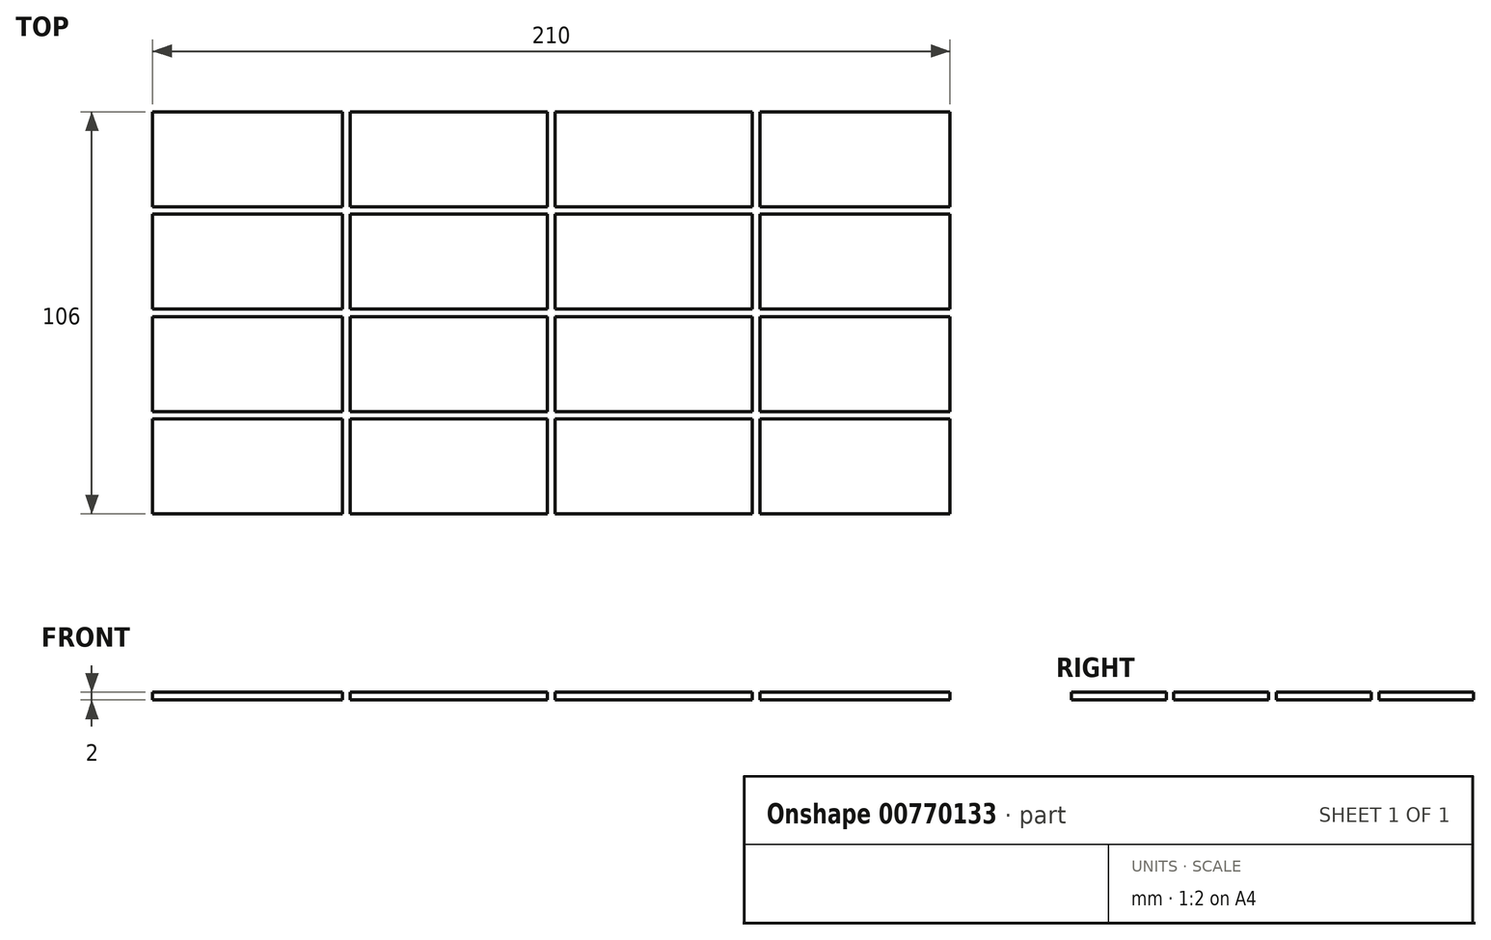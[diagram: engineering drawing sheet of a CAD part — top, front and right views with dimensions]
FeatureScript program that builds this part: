
annotation { "Feature Type Name" : "Feature", "Feature Type Description" : "" }
export const myFeature = defineFeature(function(context is Context, id is Id, definition is map)
    precondition{}
    {
        {
            var Q0;
            Q0=qCreatedBy(makeId("Top.planeOp"),FACE);
            var sketch = newSketch(context, id + "F0", { "sketchPlane" : qUnion([Q0])});
            skLineSegment(sketch, "E0.bottom", {"start": v(-107, 55) * mm, "end": v(-57, 55) * mm});
            skLineSegment(sketch, "E0.left", {"start": v(-107, 55) * mm, "end": v(-107, 30) * mm});
            skLineSegment(sketch, "E1.bottom", {"start": v(-105, 53) * mm, "end": v(-55, 53) * mm});
            skLineSegment(sketch, "E1.top", {"start": v(-105, 1) * mm, "end": v(-55, 1) * mm});
            skLineSegment(sketch, "E1.left", {"start": v(-105, 53) * mm, "end": v(-105, 28) * mm});
            skLineSegment(sketch, "E1.right", {"start": v(-1, 53) * mm, "end": v(-1, 28) * mm});
            skLineSegment(sketch, "E2", {"start": v(0, 75.4) * mm, "end": v(0, 57) * mm, "construction": true});
            skLineSegment(sketch, "E3.top", {"start": v(-57, 57) * mm, "end": v(-51, 57) * mm});
            skLineSegment(sketch, "E3.left", {"start": v(-57, 55) * mm, "end": v(-57, 57) * mm});
            skLineSegment(sketch, "E3.right", {"start": v(-51, 55) * mm, "end": v(-51, 57) * mm});
            skLineSegment(sketch, "E4.bottom", {"start": v(-42.1, 55) * mm, "end": v(-30.4, 55) * mm});
            skLineSegment(sketch, "E5.top", {"start": v(-3, 57) * mm, "end": v(0, 57) * mm});
            skLineSegment(sketch, "E5.left", {"start": v(-3, 55) * mm, "end": v(-3, 57) * mm});
            skPoint(sketch, "E4.right.end.orphan", {"position": v(-30.4, 57) * mm});
            skLineSegment(sketch, "E6.trimOffspring", {"start": v(-51, 55) * mm, "end": v(-3, 55) * mm});
            skPoint(sketch, "E7", {"position": v(-55, 53) * mm});
            skPoint(sketch, "E8", {"position": v(-53, 53) * mm});
            skLineSegment(sketch, "E9", {"start": v(-55, 53) * mm, "end": v(-55, 28) * mm});
            skLineSegment(sketch, "E10", {"start": v(-53, 53) * mm, "end": v(-53, 28) * mm});
            skPoint(sketch, "E10.endSnap0", {"position": v(-53, 1) * mm});
            skLineSegment(sketch, "E11.trimOffspring", {"start": v(-53, 1) * mm, "end": v(-1, 1) * mm});
            skLineSegment(sketch, "E12", {"start": v(-55, 53) * mm, "end": v(-55, 55) * mm});
            skLineSegment(sketch, "E13", {"start": v(-55, 55) * mm, "end": v(-53, 55) * mm});
            skLineSegment(sketch, "E14", {"start": v(-53, 55) * mm, "end": v(-53, 53) * mm});
            skLineSegment(sketch, "E15.trimOffspring", {"start": v(-53, 53) * mm, "end": v(-1, 53) * mm});
            skLineSegment(sketch, "E16", {"start": v(-1, 53) * mm, "end": v(-1, 55) * mm});
            skPoint(sketch, "E16.endSnap0", {"position": v(-27, 55) * mm});
            skLineSegment(sketch, "E17", {"start": v(-1, 55) * mm, "end": v(0, 55) * mm});
            skPoint(sketch, "E18", {"position": v(-105, 28) * mm});
            skLineSegment(sketch, "E19.bottom", {"start": v(-107, 30) * mm, "end": v(-109, 30) * mm});
            skLineSegment(sketch, "E19.top", {"start": v(-107, 24) * mm, "end": v(-109, 24) * mm});
            skLineSegment(sketch, "E19.left", {"start": v(-107, 28) * mm, "end": v(-107, 26) * mm});
            skLineSegment(sketch, "E19.right", {"start": v(-109, 30) * mm, "end": v(-109, 24) * mm});
            skLineSegment(sketch, "E20.left", {"start": v(-105, 53) * mm, "end": v(-105, 30) * mm});
            skLineSegment(sketch, "E20.right", {"start": v(-107, 53) * mm, "end": v(-107, 30) * mm});
            skLineSegment(sketch, "E21", {"start": v(-107, 28) * mm, "end": v(-55, 28) * mm});
            skLineSegment(sketch, "E22", {"start": v(-107, 26) * mm, "end": v(-55, 26) * mm});
            skLineSegment(sketch, "E23.trimOffspring", {"start": v(-105, 26) * mm, "end": v(-105, 1) * mm});
            skLineSegment(sketch, "E24.trimOffspring", {"start": v(-107, 24) * mm, "end": v(-107, 3) * mm});
            skLineSegment(sketch, "E25.trimOffspring", {"start": v(-107, 0) * mm, "end": v(-145.29, 0) * mm, "construction": true});
            skLineSegment(sketch, "E26.trimOffspring", {"start": v(-53, 26) * mm, "end": v(-1, 26) * mm});
            skLineSegment(sketch, "E27.trimOffspring", {"start": v(-53, 28) * mm, "end": v(-1, 28) * mm});
            skLineSegment(sketch, "E28.trimOffspring", {"start": v(-55, 26) * mm, "end": v(-55, 1) * mm});
            skLineSegment(sketch, "E29.trimOffspring", {"start": v(-53, 26) * mm, "end": v(-53, 1) * mm});
            skLineSegment(sketch, "E30.trimOffspring", {"start": v(-1, 26) * mm, "end": v(-1, 1) * mm});
            skPoint(sketch, "E31.orphan", {"position": v(0, 28) * mm});
            skPoint(sketch, "E32.orphan", {"position": v(0, 26) * mm});
            skLineSegment(sketch, "E33.MirrorCS", {"start": v(55, 55) * mm, "end": v(53, 55) * mm});
            skLineSegment(sketch, "E34.MirrorCS", {"start": v(107, 28) * mm, "end": v(107, 26) * mm});
            skLineSegment(sketch, "E35.MirrorCS", {"start": v(55, 53) * mm, "end": v(55, 55) * mm});
            skLineSegment(sketch, "E36.MirrorCS", {"start": v(53, 55) * mm, "end": v(53, 53) * mm});
            skLineSegment(sketch, "E37.MirrorCS", {"start": v(1, 55) * mm, "end": v(0, 55) * mm});
            skLineSegment(sketch, "E38.MirrorCS", {"start": v(1, 53) * mm, "end": v(1, 55) * mm});
            skLineSegment(sketch, "E39.MirrorCS", {"start": v(107, 30) * mm, "end": v(109, 30) * mm});
            skLineSegment(sketch, "E40.MirrorCS", {"start": v(51, 55) * mm, "end": v(51, 57) * mm});
            skLineSegment(sketch, "E41.MirrorCS", {"start": v(3, 55) * mm, "end": v(3, 57) * mm});
            skLineSegment(sketch, "E42.MirrorCS", {"start": v(57, 55) * mm, "end": v(57, 57) * mm});
            skLineSegment(sketch, "E43.MirrorCS", {"start": v(107, 24) * mm, "end": v(109, 24) * mm});
            skLineSegment(sketch, "E44.MirrorCS", {"start": v(105, 53) * mm, "end": v(105, 30) * mm});
            skLineSegment(sketch, "E45.MirrorCS", {"start": v(42.1, 55) * mm, "end": v(30.4, 55) * mm});
            skLineSegment(sketch, "E46.MirrorCS", {"start": v(107, 53) * mm, "end": v(107, 30) * mm});
            skLineSegment(sketch, "E47.MirrorCS", {"start": v(55, 26) * mm, "end": v(55, 1) * mm});
            skLineSegment(sketch, "E48.MirrorCS", {"start": v(53, 28) * mm, "end": v(1, 28) * mm});
            skPoint(sketch, "E49.MirrorP", {"position": v(105, 28) * mm});
            skLineSegment(sketch, "E50.MirrorCS", {"start": v(53, 53) * mm, "end": v(53, 28) * mm});
            skPoint(sketch, "E51.MirrorP", {"position": v(55, 53) * mm});
            skLineSegment(sketch, "E52.MirrorCS", {"start": v(3, 57) * mm, "end": v(0, 57) * mm});
            skLineSegment(sketch, "E53.MirrorCS", {"start": v(107, 28) * mm, "end": v(55, 28) * mm});
            skLineSegment(sketch, "E54.MirrorCS", {"start": v(53, 53) * mm, "end": v(1, 53) * mm});
            skLineSegment(sketch, "E55.MirrorCS", {"start": v(1, 53) * mm, "end": v(1, 28) * mm});
            skLineSegment(sketch, "E56.MirrorCS", {"start": v(105, 53) * mm, "end": v(55, 53) * mm});
            skLineSegment(sketch, "E57.MirrorCS", {"start": v(105, 26) * mm, "end": v(105, 1) * mm});
            skLineSegment(sketch, "E58.MirrorCS", {"start": v(107, 55) * mm, "end": v(57, 55) * mm});
            skLineSegment(sketch, "E59.MirrorCS", {"start": v(107, 26) * mm, "end": v(55, 26) * mm});
            skPoint(sketch, "E60.MirrorP", {"position": v(53, 53) * mm});
            skLineSegment(sketch, "E61.MirrorCS", {"start": v(57, 57) * mm, "end": v(51, 57) * mm});
            skLineSegment(sketch, "E62.MirrorCS", {"start": v(53, 26) * mm, "end": v(53, 1) * mm});
            skLineSegment(sketch, "E63.MirrorCS", {"start": v(105, 53) * mm, "end": v(105, 28) * mm});
            skLineSegment(sketch, "E64.MirrorCS", {"start": v(53, 26) * mm, "end": v(1, 26) * mm});
            skLineSegment(sketch, "E65.MirrorCS", {"start": v(55, 53) * mm, "end": v(55, 28) * mm});
            skLineSegment(sketch, "E66.MirrorCS", {"start": v(53, 1) * mm, "end": v(1, 1) * mm});
            skLineSegment(sketch, "E67.MirrorCS", {"start": v(1, 26) * mm, "end": v(1, 1) * mm});
            skPoint(sketch, "E68.MirrorP", {"position": v(53, 1) * mm});
            skPoint(sketch, "E69.MirrorP", {"position": v(30.4, 57) * mm});
            skPoint(sketch, "E70.MirrorP", {"position": v(27, 55) * mm});
            skLineSegment(sketch, "E71.MirrorCS", {"start": v(107, 24) * mm, "end": v(107, 0) * mm});
            skLineSegment(sketch, "E72.MirrorCS", {"start": v(105, 1) * mm, "end": v(55, 1) * mm});
            skLineSegment(sketch, "E73.MirrorCS", {"start": v(51, 55) * mm, "end": v(3, 55) * mm});
            skLineSegment(sketch, "E74.MirrorCS", {"start": v(109, 30) * mm, "end": v(109, 24) * mm});
            skLineSegment(sketch, "E75.MirrorCS", {"start": v(107, 55) * mm, "end": v(107, 30) * mm});
            skLineSegment(sketch, "E76.MirrorCS", {"start": v(-1, -55) * mm, "end": v(0, -55) * mm});
            skLineSegment(sketch, "E77.MirrorCS", {"start": v(1, -53) * mm, "end": v(1, -55) * mm});
            skLineSegment(sketch, "E78.MirrorCS", {"start": v(-1, -53) * mm, "end": v(-1, -55) * mm});
            skLineSegment(sketch, "E79.MirrorCS", {"start": v(1, -55) * mm, "end": v(0, -55) * mm});
            skLineSegment(sketch, "E80.MirrorCS", {"start": v(-3, -55) * mm, "end": v(-3, -57) * mm});
            skLineSegment(sketch, "E81.MirrorCS", {"start": v(-3, -57) * mm, "end": v(0, -57) * mm});
            skLineSegment(sketch, "E82.MirrorCS", {"start": v(-107, -28) * mm, "end": v(-107, -26) * mm});
            skLineSegment(sketch, "E83.MirrorCS", {"start": v(53, -55) * mm, "end": v(53, -53) * mm});
            skLineSegment(sketch, "E84.MirrorCS", {"start": v(-53, -55) * mm, "end": v(-53, -53) * mm});
            skLineSegment(sketch, "E85.MirrorCS", {"start": v(57, -55) * mm, "end": v(57, -57) * mm});
            skLineSegment(sketch, "E86.MirrorCS", {"start": v(-51, -55) * mm, "end": v(-51, -57) * mm});
            skLineSegment(sketch, "E87.MirrorCS", {"start": v(-57, -55) * mm, "end": v(-57, -57) * mm});
            skLineSegment(sketch, "E88.MirrorCS", {"start": v(-57, -57) * mm, "end": v(-51, -57) * mm});
            skLineSegment(sketch, "E89.MirrorCS", {"start": v(3, -57) * mm, "end": v(0, -57) * mm});
            skLineSegment(sketch, "E90.MirrorCS", {"start": v(-55, -55) * mm, "end": v(-53, -55) * mm});
            skLineSegment(sketch, "E91.MirrorCS", {"start": v(55, -53) * mm, "end": v(55, -55) * mm});
            skLineSegment(sketch, "E92.MirrorCS", {"start": v(-107, -30) * mm, "end": v(-109, -30) * mm});
            skLineSegment(sketch, "E93.MirrorCS", {"start": v(51, -55) * mm, "end": v(51, -57) * mm});
            skLineSegment(sketch, "E94.MirrorCS", {"start": v(-55, -53) * mm, "end": v(-55, -55) * mm});
            skLineSegment(sketch, "E95.MirrorCS", {"start": v(55, -55) * mm, "end": v(53, -55) * mm});
            skLineSegment(sketch, "E96.MirrorCS", {"start": v(107, -28) * mm, "end": v(107, -26) * mm});
            skLineSegment(sketch, "E97.MirrorCS", {"start": v(57, -57) * mm, "end": v(51, -57) * mm});
            skLineSegment(sketch, "E98.MirrorCS", {"start": v(107, -24) * mm, "end": v(109, -24) * mm});
            skLineSegment(sketch, "E99.MirrorCS", {"start": v(3, -55) * mm, "end": v(3, -57) * mm});
            skLineSegment(sketch, "E100.MirrorCS", {"start": v(109, -30) * mm, "end": v(109, -24) * mm});
            skLineSegment(sketch, "E101.MirrorCS", {"start": v(-107, -24) * mm, "end": v(-109, -24) * mm});
            skLineSegment(sketch, "E102.MirrorCS", {"start": v(-109, -30) * mm, "end": v(-109, -24) * mm});
            skLineSegment(sketch, "E103.MirrorCS", {"start": v(107, -30) * mm, "end": v(109, -30) * mm});
            skLineSegment(sketch, "E104.MirrorCS", {"start": v(105, -53) * mm, "end": v(105, -30) * mm});
            skLineSegment(sketch, "E105.MirrorCS", {"start": v(-107, -53) * mm, "end": v(-107, -30) * mm});
            skLineSegment(sketch, "E106.MirrorCS", {"start": v(-105, -53) * mm, "end": v(-105, -30) * mm});
            skLineSegment(sketch, "E107.MirrorCS", {"start": v(-1, -26) * mm, "end": v(-1, -1) * mm});
            skLineSegment(sketch, "E108.MirrorCS", {"start": v(-42.1, -55) * mm, "end": v(-30.4, -55) * mm});
            skLineSegment(sketch, "E109.MirrorCS", {"start": v(42.1, -55) * mm, "end": v(30.4, -55) * mm});
            skLineSegment(sketch, "E110.MirrorCS", {"start": v(107, -53) * mm, "end": v(107, -30) * mm});
            skLineSegment(sketch, "E111.MirrorCS", {"start": v(-107, -26) * mm, "end": v(-55, -26) * mm});
            skLineSegment(sketch, "E112.MirrorCS", {"start": v(1, -53) * mm, "end": v(1, -28) * mm});
            skLineSegment(sketch, "E113.MirrorCS", {"start": v(51, -55) * mm, "end": v(3, -55) * mm});
            skLineSegment(sketch, "E114.MirrorCS", {"start": v(-55, -53) * mm, "end": v(-55, -28) * mm});
            skLineSegment(sketch, "E115.MirrorCS", {"start": v(53, -26) * mm, "end": v(53, -1) * mm});
            skLineSegment(sketch, "E116.MirrorCS", {"start": v(-53, -28) * mm, "end": v(-1, -28) * mm});
            skPoint(sketch, "E117.MirrorP", {"position": v(105, -28) * mm});
            skLineSegment(sketch, "E118.MirrorCS", {"start": v(-107, -28) * mm, "end": v(-55, -28) * mm});
            skLineSegment(sketch, "E119.MirrorCS", {"start": v(53, -53) * mm, "end": v(1, -53) * mm});
            skLineSegment(sketch, "E120.MirrorCS", {"start": v(105, -1) * mm, "end": v(55, -1) * mm});
            skLineSegment(sketch, "E121.MirrorCS", {"start": v(-51, -55) * mm, "end": v(-3, -55) * mm});
            skPoint(sketch, "E122.MirrorP", {"position": v(0, -26) * mm});
            skLineSegment(sketch, "E123.MirrorCS", {"start": v(-53, -53) * mm, "end": v(-1, -53) * mm});
            skLineSegment(sketch, "E124.MirrorCS", {"start": v(-53, -26) * mm, "end": v(-1, -26) * mm});
            skLineSegment(sketch, "E125.MirrorCS", {"start": v(107, -28) * mm, "end": v(55, -28) * mm});
            skLineSegment(sketch, "E126.MirrorCS", {"start": v(107, -24) * mm, "end": v(107, 0) * mm});
            skPoint(sketch, "E127.MirrorP", {"position": v(0, -28) * mm});
            skPoint(sketch, "E128.MirrorP", {"position": v(27, -55) * mm});
            skLineSegment(sketch, "E129.MirrorCS", {"start": v(-1, -53) * mm, "end": v(-1, -28) * mm});
            skLineSegment(sketch, "E130.MirrorCS", {"start": v(-105, -53) * mm, "end": v(-105, -28) * mm});
            skLineSegment(sketch, "E131.MirrorCS", {"start": v(-105, -1) * mm, "end": v(-55, -1) * mm});
            skLineSegment(sketch, "E132.MirrorCS", {"start": v(-105, -53) * mm, "end": v(-55, -53) * mm});
            skLineSegment(sketch, "E133.MirrorCS", {"start": v(-107, -55) * mm, "end": v(-107, -30) * mm});
            skLineSegment(sketch, "E134.MirrorCS", {"start": v(-107, -55) * mm, "end": v(-57, -55) * mm});
            skLineSegment(sketch, "E135.MirrorCS", {"start": v(107, -26) * mm, "end": v(55, -26) * mm});
            skPoint(sketch, "E136.MirrorP", {"position": v(55, -53) * mm});
            skPoint(sketch, "E137.MirrorP", {"position": v(-27, -55) * mm});
            skLineSegment(sketch, "E138.MirrorCS", {"start": v(-53, -53) * mm, "end": v(-53, -28) * mm});
            skPoint(sketch, "E139.MirrorP", {"position": v(53, -1) * mm});
            skPoint(sketch, "E140.MirrorP", {"position": v(30.4, -57) * mm});
            skLineSegment(sketch, "E141.MirrorCS", {"start": v(1, -26) * mm, "end": v(1, -1) * mm});
            skLineSegment(sketch, "E142.MirrorCS", {"start": v(105, -53) * mm, "end": v(105, -28) * mm});
            skPoint(sketch, "E143.MirrorP", {"position": v(-53, -1) * mm});
            skPoint(sketch, "E144.MirrorP", {"position": v(-53, -53) * mm});
            skLineSegment(sketch, "E145.MirrorCS", {"start": v(55, -53) * mm, "end": v(55, -28) * mm});
            skPoint(sketch, "E146.MirrorP", {"position": v(-105, -28) * mm});
            skLineSegment(sketch, "E147.MirrorCS", {"start": v(55, -26) * mm, "end": v(55, -1) * mm});
            skLineSegment(sketch, "E148.MirrorCS", {"start": v(53, -26) * mm, "end": v(1, -26) * mm});
            skPoint(sketch, "E149.MirrorP", {"position": v(-55, -53) * mm});
            skLineSegment(sketch, "E150.MirrorCS", {"start": v(53, -53) * mm, "end": v(53, -28) * mm});
            skPoint(sketch, "E151.MirrorP", {"position": v(53, -53) * mm});
            skLineSegment(sketch, "E152.MirrorCS", {"start": v(-105, -26) * mm, "end": v(-105, -1) * mm});
            skLineSegment(sketch, "E153.MirrorCS", {"start": v(-53, -1) * mm, "end": v(-1, -1) * mm});
            skPoint(sketch, "E154.MirrorP", {"position": v(-30.4, -57) * mm});
            skLineSegment(sketch, "E155.MirrorCS", {"start": v(107, -55) * mm, "end": v(107, -30) * mm});
            skLineSegment(sketch, "E156.MirrorCS", {"start": v(-107, -24) * mm, "end": v(-107, -3) * mm});
            skLineSegment(sketch, "E157.MirrorCS", {"start": v(107, -55) * mm, "end": v(57, -55) * mm});
            skLineSegment(sketch, "E158.MirrorCS", {"start": v(-53, -26) * mm, "end": v(-53, -1) * mm});
            skLineSegment(sketch, "E159.MirrorCS", {"start": v(-55, -26) * mm, "end": v(-55, -1) * mm});
            skLineSegment(sketch, "E160.MirrorCS", {"start": v(53, -1) * mm, "end": v(1, -1) * mm});
            skLineSegment(sketch, "E161.MirrorCS", {"start": v(53, -28) * mm, "end": v(1, -28) * mm});
            skLineSegment(sketch, "E162.MirrorCS", {"start": v(105, -53) * mm, "end": v(55, -53) * mm});
            skLineSegment(sketch, "E163.MirrorCS", {"start": v(105, -26) * mm, "end": v(105, -1) * mm});
            skPoint(sketch, "E5.right.start.orphan", {"position": v(0, 55) * mm});
            skPoint(sketch, "E164.MirrorCS.start.orphan", {"position": v(0, -55) * mm});
            skPoint(sketch, "E165.orphan", {"position": v(23.42, 0) * mm});
            skPoint(sketch, "E166.orphan", {"position": v(0, 0) * mm});
            skPoint(sketch, "E167.MirrorCS.start.orphan", {"position": v(53, 0) * mm});
            skPoint(sketch, "E168.MirrorCS.end.orphan", {"position": v(55, 0) * mm});
            skPoint(sketch, "E169.trimOffspring.start.orphan", {"position": v(-53, 0) * mm});
            skPoint(sketch, "E0.top.end.orphan", {"position": v(-55, 0) * mm});
            skLineSegment(sketch, "E170", {"start": v(-107, 3) * mm, "end": v(-109, 3) * mm});
            skLineSegment(sketch, "E171", {"start": v(-109, 3) * mm, "end": v(-109, 0) * mm});
            skLineSegment(sketch, "E172", {"start": v(-109, 0) * mm, "end": v(-109, -3) * mm});
            skLineSegment(sketch, "E173", {"start": v(-109, -3) * mm, "end": v(-107, -3) * mm});
            skLineSegment(sketch, "E174", {"start": v(-105, 1) * mm, "end": v(-107, 1) * mm});
            skLineSegment(sketch, "E175", {"start": v(-105, -1) * mm, "end": v(-107, -1) * mm});
            skLineSegment(sketch, "E176.trimOffspring", {"start": v(-107, 1) * mm, "end": v(-107, 0) * mm});
            skLineSegment(sketch, "E177.trimOffspring", {"start": v(-107, -1) * mm, "end": v(-107, 0) * mm});
            skLineSegment(sketch, "E178", {"start": v(-107, 1) * mm, "end": v(-107, -1) * mm});
            skSolve(sketch);
        }
        {
            var Q0;
            Q0=makeQuery(id+"F0.imprint","IMPRINT",FACE,{"disambiguationData":[TD([[makeQuery(id+"F0.imprint","IMPRINT",EDGE,{"derivedFrom":sQuery(id+"F0.wireOp",EDGE,"E1.bottom")}),-1.0]])]});
            var Q1;
            Q1=makeQuery(id+"F0.imprint","IMPRINT",FACE,{"disambiguationData":[TD([[makeQuery(id+"F0.imprint","IMPRINT",EDGE,{"derivedFrom":sQuery(id+"F0.wireOp",EDGE,"E1.right")}),-1.0]])]});
            var Q2;
            Q2=makeQuery(id+"F0.imprint","IMPRINT",FACE,{"disambiguationData":[TD([[makeQuery(id+"F0.imprint","IMPRINT",EDGE,{"derivedFrom":sQuery(id+"F0.wireOp",EDGE,"E48.MirrorCS")}),-1.0]])]});
            var Q3;
            Q3=makeQuery(id+"F0.imprint","IMPRINT",FACE,{"disambiguationData":[TD([[makeQuery(id+"F0.imprint","IMPRINT",EDGE,{"derivedFrom":sQuery(id+"F0.wireOp",EDGE,"E62.MirrorCS")}),-1.0]])]});
            var Q4;
            Q4=makeQuery(id+"F0.imprint","IMPRINT",FACE,{"disambiguationData":[TD([[makeQuery(id+"F0.imprint","IMPRINT",EDGE,{"derivedFrom":sQuery(id+"F0.wireOp",EDGE,"E11.trimOffspring")}),1.0]])]});
            var Q5;
            Q5=makeQuery(id+"F0.imprint","IMPRINT",FACE,{"disambiguationData":[TD([[makeQuery(id+"F0.imprint","IMPRINT",EDGE,{"derivedFrom":sQuery(id+"F0.wireOp",EDGE,"E1.top")}),1.0]])]});
            var Q6;
            Q6=makeQuery(id+"F0.imprint","IMPRINT",FACE,{"disambiguationData":[TD([[makeQuery(id+"F0.imprint","IMPRINT",EDGE,{"derivedFrom":sQuery(id+"F0.wireOp",EDGE,"E131.MirrorCS")}),-1.0]])]});
            var Q7;
            Q7=makeQuery(id+"F0.imprint","IMPRINT",FACE,{"disambiguationData":[TD([[makeQuery(id+"F0.imprint","IMPRINT",EDGE,{"derivedFrom":sQuery(id+"F0.wireOp",EDGE,"E107.MirrorCS")}),1.0]])]});
            var Q8;
            Q8=makeQuery(id+"F0.imprint","IMPRINT",FACE,{"disambiguationData":[TD([[makeQuery(id+"F0.imprint","IMPRINT",EDGE,{"derivedFrom":sQuery(id+"F0.wireOp",EDGE,"E115.MirrorCS")}),1.0]])]});
            var Q9;
            {var subQ1=sQuery(id+"F0.wireOp",EDGE,"E56.MirrorCS");Q9=makeQuery(id+"F0.imprint","IMPRINT",FACE,{"disambiguationData":[TD([[makeQuery(id+"F0.imprint","IMPRINT",EDGE,{"derivedFrom":subQ1}),1.0]])]});}
            var Q10;
            {var subQ0=sQuery(id+"F0.wireOp",EDGE,"E47.MirrorCS");Q10=makeQuery(id+"F0.imprint","IMPRINT",FACE,{"disambiguationData":[TD([[makeQuery(id+"F0.imprint","IMPRINT",EDGE,{"derivedFrom":subQ0}),1.0]])]});}
            var Q11;
            Q11=makeQuery(id+"F0.imprint","IMPRINT",FACE,{"disambiguationData":[TD([[makeQuery(id+"F0.imprint","IMPRINT",EDGE,{"derivedFrom":sQuery(id+"F0.wireOp",EDGE,"E120.MirrorCS")}),1.0]])]});
            var Q12;
            {var subQ0=sQuery(id+"F0.wireOp",EDGE,"E145.MirrorCS");Q12=makeQuery(id+"F0.imprint","IMPRINT",FACE,{"disambiguationData":[TD([[makeQuery(id+"F0.imprint","IMPRINT",EDGE,{"derivedFrom":subQ0}),-1.0]])]});}
            var Q13;
            Q13=makeQuery(id+"F0.imprint","IMPRINT",FACE,{"disambiguationData":[TD([[makeQuery(id+"F0.imprint","IMPRINT",EDGE,{"derivedFrom":sQuery(id+"F0.wireOp",EDGE,"E112.MirrorCS")}),-1.0]])]});
            var Q14;
            Q14=makeQuery(id+"F0.imprint","IMPRINT",FACE,{"disambiguationData":[TD([[makeQuery(id+"F0.imprint","IMPRINT",EDGE,{"derivedFrom":sQuery(id+"F0.wireOp",EDGE,"E116.MirrorCS")}),-1.0]])]});
            var Q15;
            {var subQ5=sQuery(id+"F0.wireOp",EDGE,"E114.MirrorCS");Q15=makeQuery(id+"F0.imprint","IMPRINT",FACE,{"disambiguationData":[TD([[makeQuery(id+"F0.imprint","IMPRINT",EDGE,{"derivedFrom":subQ5}),1.0]])]});}
            extrude(context, id + "F1", {"entities" : qUnion([Q0, Q1, Q2, Q3, Q4, Q5, Q6, Q7, Q8, Q9, Q10, Q11, Q12, Q13, Q14, Q15]), "depth" : 2 * mm, "offsetDistance" : 25 * mm});
        }
    });
